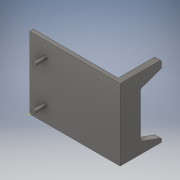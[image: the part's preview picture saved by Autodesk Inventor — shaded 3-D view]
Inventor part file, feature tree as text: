
AUTODESK INVENTOR PART (.ipt)
format: ipt  version: 2018 (Build 220112000, 112)  size: 153,088 bytes
history: native  units: in
note: dims shown in document units (in); Inventor stores cm internally (conversion verified against a paired STEP export)
features: sketch x5, extrude x4, thread x2, fillet x1
ambient origin geometry x8: Origin, YZ Plane, XZ Plane, XY Plane, X Axis, Y Axis, Z Axis, Center Point
bodies: Solid1 (feature_tree)
feature tree (12):
  extrude  "Extrusion1"  Depth=4.75in
  sketch  "Sketch2"  dims[d2=0.25in d3=0.0in d18=1.0in d20=1.0in d23=1.0in]
  sketch  "Sketch3"  dims[d24=1.0331in d25=0.75in d26=0.0in]
  extrude  "Extrusion4"  Depth=1.0in
  thread  "Thread5"  [1 undecoded]
  thread  "Thread6"  [1 undecoded]
  extrude  "Extrusion6"  Depth=0.75in TaperAngle=0.0deg
  extrude  "Extrusion7"  Depth=1.0in TaperAngle=0.0deg
  fillet  "Fillet1"  Radius=2.75in
  sketch  "Sketch1"  dims[d0=6.0in d1=4.75in]
  sketch  "Sketch7"  dims[d27=1.0in d28=0.0in d29=1.0in d30=0.0in d31=2.75in]
  sketch  "Sketch8"  dims[d32=0.25in d36=0.375in d37=2.5in d38=0.0in d39=0.5in d40=0.5in d41=1.35in d42=1.35in d43=1.35in d44=1.35in d45=2.5in d46=0.0in d47=0.125in]
note: 2 required parameter values undecoded (feature->parameter linkage not recoverable at this tier; creation-order binding heuristic only, values carry confidence <= 0.55)
